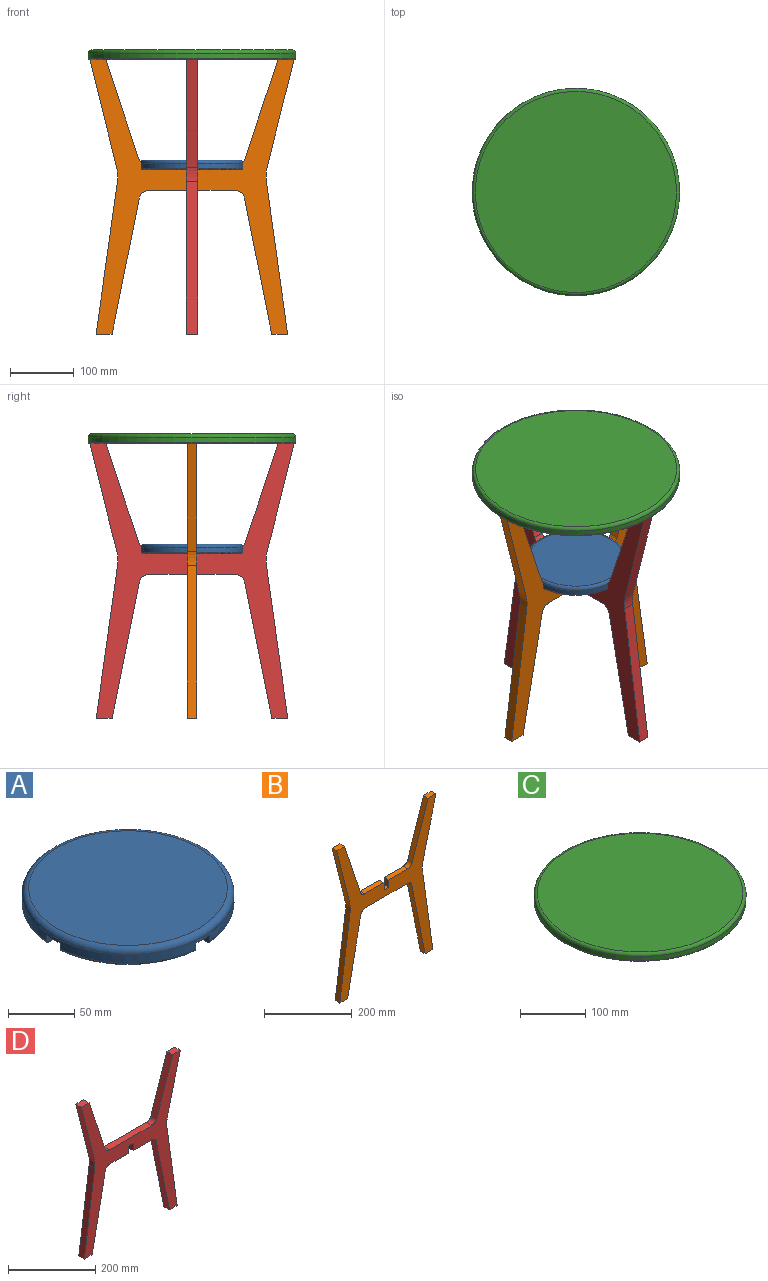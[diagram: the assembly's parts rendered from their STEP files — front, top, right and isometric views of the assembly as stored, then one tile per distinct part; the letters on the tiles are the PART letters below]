
ASSEMBLY  parts=4 mates=3
PART A: 20 faces, bbox 173.2x173.2x15 mm
  f0: plane 70.14x70.14mm, normal (0,0,-1), area 3666.4mm2, adj f3,f12,f13
  f1: plane 70.14x70.14mm, normal (0,0,-1), area 3666.4mm2, adj f6,f16,f17
  f2: plane 70.14x70.14mm, normal (0,0,-1), area 3666.4mm2, adj f5,f11,f18
  f3: torus R=78mm, axis (0,0,-1), area 344mm2, adj f0,f7,f12,f13
  f4: torus R=78mm, axis (0,0,-1), area 344mm2, adj f7,f9,f14,f15
  f5: torus R=78mm, axis (0,0,-1), area 344mm2, adj f2,f7,f11,f18
  f6: torus R=78mm, axis (0,0,-1), area 344mm2, adj f1,f7,f16,f17
  f7: cylinder r=80mm len=160mm, axis (0,0,-1), area 3690.8mm2, adj f3,f4,f5,f6,f10,f11,f12,f13
  f8: plane 150x150mm, normal (0,0,1), area 17671.5mm2, adj f10
  f9: plane 70.14x70.14mm, normal (0,0,-1), area 3666.4mm2, adj f4,f14,f15
  f10: torus R=75mm, axis (0,0,-1), area 3858.2mm2, adj f7,f8
  f11: plane 72.15x7.5mm, normal (-1,0,0), area 540.2mm2, adj f2,f5,f7,f18,f19
  f12: plane 72.15x7.5mm, normal (1,0,0), area 540.2mm2, adj f0,f3,f7,f13,f19
  f13: plane 72.15x7.5mm, normal (0,1,0), area 540.2mm2, adj f0,f3,f7,f12,f19
  f14: plane 72.15x7.5mm, normal (0,-1,0), area 540.2mm2, adj f4,f7,f9,f15,f19
  f15: plane 72.15x7.5mm, normal (1,0,0), area 540.2mm2, adj f4,f7,f9,f14,f19
  f16: plane 72.15x7.5mm, normal (-1,0,0), area 540.2mm2, adj f1,f6,f7,f17,f19
  f17: plane 72.15x7.5mm, normal (0,-1,0), area 540.2mm2, adj f1,f6,f7,f16,f19
  f18: plane 72.15x7.5mm, normal (0,1,0), area 540.2mm2, adj f2,f5,f7,f11,f19
  f19: plane 160x160mm, normal (0,0,-1), area 4568mm2, adj f7,f11,f12,f13,f14,f15,f16,f17
PART B: 26 faces, bbox 320x15x430 mm
  f0: plane 135.41x15mm, normal (0,0,-1), area 2031.1mm2, adj f1,f23,f24,f25
  f1: cylinder r=15mm len=15mm, axis (0,1,0), area 309mm2, adj f0,f2,f24,f25
  f2: plane 212.94x42.59mm, normal (-0.98,0,-0.2), area 3257.4mm2, adj f1,f3,f24,f25
  f3: plane 25x15mm, normal (0,0,-1), area 375mm2, adj f2,f4,f24,f25
  f4: plane 238.45x33.38mm, normal (0.99,0,0.14), area 3611.6mm2, adj f3,f5,f24,f25
  f5: cylinder r=60mm len=22.87mm, axis (0,1,0), area 345.7mm2, adj f4,f6,f24,f25
  f6: plane 168.68x42.17mm, normal (0.97,0,-0.24), area 2608.1mm2, adj f5,f7,f24,f25
  f7: plane 25x15mm, normal (0,0,1), area 375mm2, adj f6,f8,f24,f25
  f8: plane 154.74x51.58mm, normal (-0.95,0,0.32), area 2446.7mm2, adj f7,f9,f24,f25
  f9: cylinder r=15mm len=15mm, axis (0,1,0), area 281mm2, adj f8,f10,f24,f25
  f10: plane 61.69x15mm, normal (0,0,1), area 925.3mm2, adj f9,f11,f24,f25
  f11: plane 20x15mm, normal (-1,0,0), area 300mm2, adj f10,f12,f24,f25
  f12: plane 15x15mm, normal (0,0,1), area 225mm2, adj f11,f13,f24,f25
  f13: plane 20x15mm, normal (1,0,0), area 300mm2, adj f12,f14,f24,f25
  f14: plane 61.69x15mm, normal (0,0,1), area 925.3mm2, adj f13,f15,f24,f25
  f15: cylinder r=15mm len=15mm, axis (0,1,0), area 281mm2, adj f14,f16,f24,f25
  f16: plane 154.74x51.58mm, normal (0.95,0,0.32), area 2446.7mm2, adj f15,f17,f24,f25
  f17: plane 25x15mm, normal (0,0,1), area 375mm2, adj f16,f18,f24,f25
  f18: plane 168.68x42.17mm, normal (-0.97,0,-0.24), area 2608.1mm2, adj f17,f19,f24,f25
  f19: cylinder r=60mm len=22.87mm, axis (0,1,0), area 345.7mm2, adj f18,f20,f24,f25
  f20: plane 238.45x33.38mm, normal (-0.99,0,0.14), area 3611.6mm2, adj f19,f21,f24,f25
  f21: plane 25x15mm, normal (0,0,-1), area 375mm2, adj f20,f22,f24,f25
  f22: plane 212.94x42.59mm, normal (0.98,0,-0.2), area 3257.4mm2, adj f21,f23,f24,f25
  f23: cylinder r=15mm len=15mm, axis (0,1,0), area 309mm2, adj f0,f22,f24,f25
  f24: plane 430x320mm, normal (0,-1,0), area 33970.5mm2, adj f0,f1,f2,f3,f4,f5,f6,f7
  f25: plane 430x320mm, normal (0,1,0), area 33970.5mm2, adj f0,f1,f2,f3,f4,f5,f6,f7
PART C: 5 faces, bbox 351.8x351.8x15 mm
  f0: torus R=157.5mm, axis (0,0,1), area 7929.4mm2, adj f1,f4
  f1: plane 315x315mm, normal (0,0,1), area 77931.1mm2, adj f0
  f2: plane 321x321mm, normal (0,0,-1), area 80928.2mm2, adj f3
  f3: torus R=160.5mm, axis (0,0,1), area 3193.3mm2, adj f2,f4
  f4: cylinder r=162.5mm len=325mm, axis (0,0,1), area 8168.1mm2, adj f0,f3
PART D: 26 faces, bbox 320x18x430 mm
  f0: plane 138.38x18mm, normal (0,0,1), area 2490.8mm2, adj f1,f23,f24,f25
  f1: cylinder r=15mm len=18mm, axis (0,1,0), area 337.2mm2, adj f0,f2,f24,f25
  f2: plane 154.74x51.58mm, normal (0.95,0,0.32), area 2936mm2, adj f1,f3,f24,f25
  f3: plane 25x18mm, normal (0,0,1), area 450mm2, adj f2,f4,f24,f25
  f4: plane 168.68x42.17mm, normal (-0.97,0,-0.24), area 3129.7mm2, adj f3,f5,f24,f25
  f5: cylinder r=60mm len=22.87mm, axis (0,1,0), area 414.8mm2, adj f4,f6,f24,f25
  f6: plane 238.45x33.38mm, normal (-0.99,0,0.14), area 4333.9mm2, adj f5,f7,f24,f25
  f7: plane 25x18mm, normal (0,0,-1), area 450mm2, adj f6,f8,f24,f25
  f8: plane 212.94x42.59mm, normal (0.98,0,-0.2), area 3908.9mm2, adj f7,f9,f24,f25
  f9: cylinder r=15mm len=18mm, axis (0,1,0), area 370.8mm2, adj f8,f10,f24,f25
  f10: plane 60.2x18mm, normal (0,0,-1), area 1083.7mm2, adj f9,f11,f24,f25
  f11: plane 20x18mm, normal (1,0,0), area 360mm2, adj f10,f12,f24,f25
  f12: plane 18x15mm, normal (0,0,-1), area 270mm2, adj f11,f13,f24,f25
  f13: plane 20x18mm, normal (-1,0,0), area 360mm2, adj f12,f14,f24,f25
  f14: plane 60.2x18mm, normal (0,0,-1), area 1083.7mm2, adj f13,f15,f24,f25
  f15: cylinder r=15mm len=18mm, axis (0,1,0), area 370.8mm2, adj f14,f16,f24,f25
  f16: plane 212.94x42.59mm, normal (-0.98,0,-0.2), area 3908.9mm2, adj f15,f17,f24,f25
  f17: plane 25x18mm, normal (0,0,-1), area 450mm2, adj f16,f18,f24,f25
  f18: plane 238.45x33.38mm, normal (0.99,0,0.14), area 4333.9mm2, adj f17,f19,f24,f25
  f19: cylinder r=60mm len=22.87mm, axis (0,1,0), area 414.8mm2, adj f18,f20,f24,f25
  f20: plane 168.68x42.17mm, normal (0.97,0,-0.24), area 3129.7mm2, adj f19,f21,f24,f25
  f21: plane 25x18mm, normal (0,0,1), area 450mm2, adj f20,f22,f24,f25
  f22: plane 154.74x51.58mm, normal (-0.95,0,0.32), area 2936mm2, adj f21,f23,f24,f25
  f23: cylinder r=15mm len=18mm, axis (0,1,0), area 337.2mm2, adj f0,f22,f24,f25
  f24: plane 430x320mm, normal (0,-1,0), area 33970.5mm2, adj f0,f1,f2,f3,f4,f5,f6,f7
  f25: plane 430x320mm, normal (0,1,0), area 33970.5mm2, adj f0,f1,f2,f3,f4,f5,f6,f7
PLACE A t=(0,0,-187.5)mm
PLACE B t=(0,0,15)mm
PLACE C t=(0,0,-15)mm
PLACE D rot(axis=(0,0,1),90deg) t=(0,0,-15)mm
MATE fastened D.f0 <-> A.f3  axis (0,0,1) through (0,0,-180)mm
MATE fastened B.f12 <-> D.f12  axis (0,0,1) through (0,0,-200)mm
MATE fastened C.f0 <-> A.f3  axis (0,0,1) through (0,0,2.5)mm
